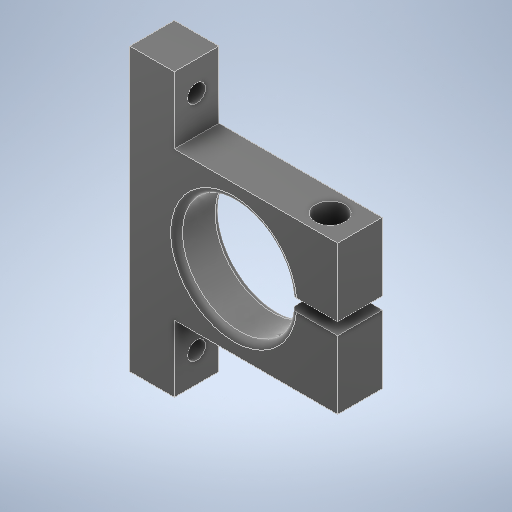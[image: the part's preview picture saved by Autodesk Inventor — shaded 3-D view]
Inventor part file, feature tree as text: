
AUTODESK INVENTOR PART (.ipt)
format: ipt  version: 2025.1 (Build 291241020, 241B)  size: 688,640 bytes
history: native  units: mm
features: sketch x5, extrude x3, mirror x3, hole x2, fillet x1
ambient origin geometry x8: Origin, YZ Plane, XZ Plane, XY Plane, X Axis, Y Axis, Z Axis, Center Point
bodies: Solid1 (feature_tree)
feature tree (14):
  extrude  "Extrusion1"  Depth=25.0mm
  mirror  "Mirror1"
  extrude  "Extrusion2"  Depth=15.0mm TaperAngle=0.0deg
  hole  "Hole1"  [1 undecoded]
  extrude  "Extrusion3"  Depth=2.0mm
  mirror  "Mirror2"
  hole  "Hole2"  [1 undecoded]
  mirror  "Mirror3"
  fillet  "Fillet1"  Radius=10.0mm
  sketch  "Sketch1"  dims[d0=15.0mm d1=25.0mm]
  sketch  "Sketch2"  dims[d2=47.5mm d4=15.0mm d5=0.0mm]
  sketch  "Sketch3"  dims[d6=38.5mm d7=35.0mm]
  sketch  "Sketch4"  dims[d8=4.0mm d9=2.0mm]
  sketch  "Sketch5"  dims[d10=5.0mm d11=0.0mm d12=7.5mm d13=10.0mm d14=6.0mm d15=6.0mm d16=4.0mm d17=2.0mm d18=90.0deg d19=8.0mm d20=20.594885mm d21=10.0mm d22=15.0mm d23=0.0mm d24=55.0mm d26=7.5mm d27=6.0mm d28=6.0mm d29=4.0mm d30=2.0mm d31=90.0deg d32=8.0mm d33=20.594885mm d34=10.0mm d35=2.0mm]
note: 2 required parameter values undecoded (feature->parameter linkage not recoverable at this tier; creation-order binding heuristic only, values carry confidence <= 0.55)
